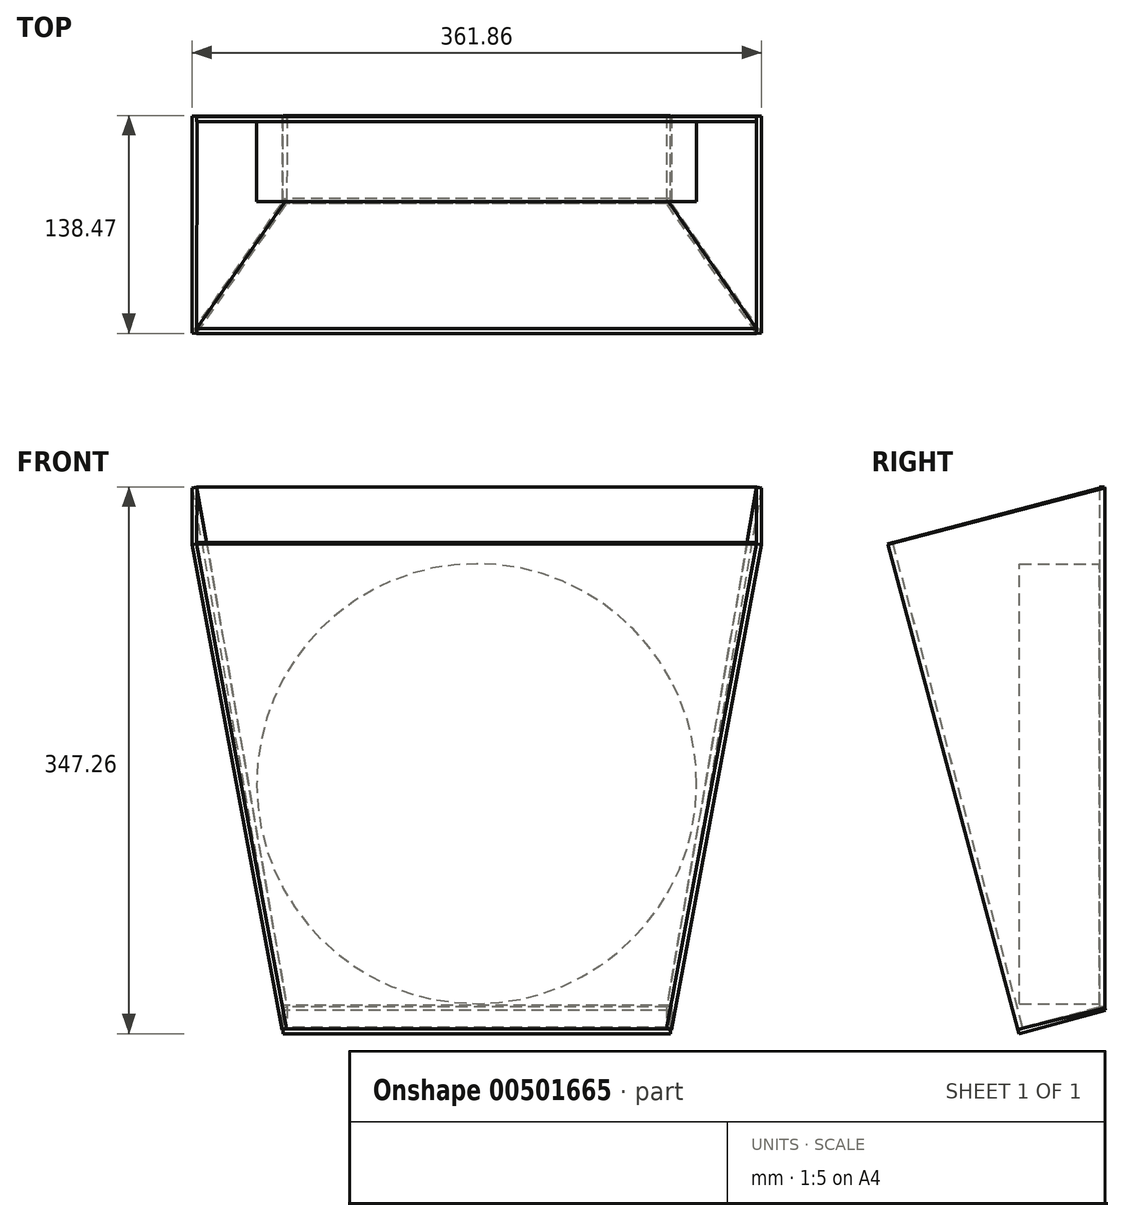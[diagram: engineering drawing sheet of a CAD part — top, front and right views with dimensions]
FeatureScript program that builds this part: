
annotation { "Feature Type Name" : "Feature", "Feature Type Description" : "" }
export const myFeature = defineFeature(function(context is Context, id is Id, definition is map)
    precondition{}
    {
        {
            var Q0;
            Q0=qCreatedBy(makeId("Right.planeOp"),FACE);
            var sketch = newSketch(context, id + "F0", { "sketchPlane" : qUnion([Q0])});
            skLineSegment(sketch, "E0.bottom", {"start": v(-164.52, 79.35) * mm, "end": v(-89.48, 66.12) * mm});
            skLineSegment(sketch, "E0.top", {"start": v(-67.49, 629.66) * mm, "end": v(7.56, 616.43) * mm});
            skLineSegment(sketch, "E0.left", {"start": v(-164.52, 79.35) * mm, "end": v(-67.49, 629.66) * mm});
            skLineSegment(sketch, "E0.right", {"start": v(-89.48, 66.12) * mm, "end": v(7.56, 616.43) * mm});
            skLineSegment(sketch, "E1.bottom", {"start": v(0, 38.1) * mm, "end": v(406.4, 38.1) * mm});
            skLineSegment(sketch, "E1.top", {"start": v(0, 546.1) * mm, "end": v(406.4, 546.1) * mm});
            skLineSegment(sketch, "E1.left", {"start": v(0, 38.1) * mm, "end": v(0, 546.1) * mm});
            skLineSegment(sketch, "E1.right", {"start": v(406.4, 38.1) * mm, "end": v(406.4, 546.1) * mm});
            skLineSegment(sketch, "E2.bottom", {"start": v(42.48, 128.48) * mm, "end": v(86.93, 128.48) * mm});
            skLineSegment(sketch, "E2.top", {"start": v(42.48, 84.03) * mm, "end": v(86.93, 84.03) * mm});
            skLineSegment(sketch, "E2.left", {"start": v(42.48, 128.48) * mm, "end": v(42.48, 84.03) * mm});
            skLineSegment(sketch, "E2.right", {"start": v(86.93, 128.48) * mm, "end": v(86.93, 84.03) * mm});
            skPoint(sketch, "E2.middle", {"position": v(64.7, 106.26) * mm});
            skSolve(sketch);
        }
        {
            var Q0;
            Q0=qCreatedBy(makeId("Front.planeOp"),FACE);
            var sketch = newSketch(context, id + "F1", { "sketchPlane" : qUnion([Q0])});
            skLineSegment(sketch, "E3.bottom", {"start": v(177.8, 596.9) * mm, "end": v(-177.8, 596.9) * mm});
            skLineSegment(sketch, "E3.top", {"start": v(120.65, 266.7) * mm, "end": v(-120.65, 266.7) * mm});
            skPoint(sketch, "E3.middle", {"position": v(0, 431.8) * mm});
            skLineSegment(sketch, "E4", {"start": v(-177.8, 596.9) * mm, "end": v(-120.65, 266.7) * mm});
            skLineSegment(sketch, "E5", {"start": v(0, 596.9) * mm, "end": v(0, 604.14) * mm, "construction": true});
            skPoint(sketch, "E5.endSnap0", {"position": v(0, 596.9) * mm});
            skLineSegment(sketch, "E6.MirrorCS", {"start": v(177.8, 596.9) * mm, "end": v(120.65, 266.7) * mm});
            skCircle(sketch, "E7", {"center": v(0, 408.44) * mm, "radius": 139.7 * mm, "construction": true});
            skCircle(sketch, "E8", {"center": v(0, 330.2) * mm, "radius": 17.46 * mm, "construction": true});
            skPoint(sketch, "E3.left.end.orphan", {"position": v(177.8, 266.7) * mm});
            skPoint(sketch, "E9.orphan", {"position": v(-177.8, 266.7) * mm});
            skSolve(sketch);
        }
        {
            var Q0;
            Q0=qSketchRegion(id+"F1",true);
            extrude(context, id + "F2", {"entities" : qUnion([Q0]), "oppositeDirection" : true, "depth" : 3.17 * mm});
        }
        {
            var Q0;
            Q0=makeQuery(id+"F1.imprint","IMPRINT",FACE,{"disambiguationData":[TD([[makeQuery(id+"F1.imprint","IMPRINT",EDGE,{"derivedFrom":sQuery(id+"F1.wireOp",EDGE,"E3.bottom")}),1.0]])]});
            var sketch = newSketch(context, id + "F3", { "sketchPlane" : qUnion([Q0])});
            skCircle(sketch, "E10.0", {"center": v(0, 408.44) * mm, "radius": 139.7 * mm});
            skSolve(sketch);
        }
        {
            var Q0;
            Q0=qSketchRegion(id+"F3",true);
            extrude(context, id + "F4", {"entities" : qUnion([Q0]), "depth" : 50.8 * mm});
        }
        {
            var Q0;
            Q0=makeQuery(id+"F4.opExtrude","CAP_FACE",FACE,{"disambiguationData":[OSD([sQuery(id+"F3.wireOp",EDGE,"E10.0")])],"isStart":false});
            var Q1;
            Q1=sQuery(id+"F1.wireOp",EDGE,"E3.top");
            cPlane(context, id + "F5", {"entities" : qUnion([Q0, Q1]), "cplaneType" : CPlaneType.LINE_ANGLE, "offset" : 25.4 * mm, "angle" : 345 * degree, "width" : 152.4 * mm, "height" : 152.4 * mm});
        }
        {
            var Q0;
            Q0=qCreatedBy(id+"F5.planeOp",FACE);
            cPlane(context, id + "F6", {"entities" : qUnion([Q0]), "cplaneType" : CPlaneType.OFFSET, "offset" : 53.97 * mm, "oppositeDirection" : true, "width" : 152.4 * mm, "height" : 152.4 * mm});
        }
        {
            var Q0;
            Q0=qCreatedBy(id+"F6.planeOp",FACE);
            var sketch = newSketch(context, id + "F7", { "sketchPlane" : qUnion([Q0])});
            skLineSegment(sketch, "E11.0", {"start": v(177.8, 576.56) * mm, "end": v(120.65, 257.61) * mm});
            skLineSegment(sketch, "E11.1", {"start": v(-177.8, 576.56) * mm, "end": v(177.8, 576.56) * mm});
            skLineSegment(sketch, "E11.2", {"start": v(-177.8, 576.56) * mm, "end": v(-120.65, 257.61) * mm});
            skLineSegment(sketch, "E11.3", {"start": v(-120.65, 257.61) * mm, "end": v(120.65, 257.61) * mm});
            skSolve(sketch);
        }
        {
            var Q0;
            Q0=makeQuery(id+"F7.imprint","IMPRINT",FACE,{"disambiguationData":[TD([[makeQuery(id+"F7.imprint","IMPRINT",EDGE,{"derivedFrom":sQuery(id+"F7.wireOp",EDGE,"E11.0")}),-1.0]])]});
            extrude(context, id + "F8", {"entities" : qUnion([Q0]), "depth" : 3.17 * mm});
        }
        {
            var Q0;
            Q0=makeQuery(id+"F8.opExtrude","SWEPT_FACE",FACE,{"disambiguationData":[OSD([sQuery(id+"F7.wireOp",EDGE,"E11.0")])]});
            var sketch = newSketch(context, id + "F9", { "sketchPlane" : qUnion([Q0])});
            skLineSegment(sketch, "E12.0", {"start": v(0.18, 618.48) * mm, "end": v(0.18, 283.37) * mm});
            skLineSegment(sketch, "E13.0", {"start": v(138.18, 582.92) * mm, "end": v(55.54, 269.6) * mm});
            skLineSegment(sketch, "E14", {"start": v(0.18, 283.37) * mm, "end": v(52.47, 270.41) * mm});
            skLineSegment(sketch, "E15", {"start": v(0.18, 618.48) * mm, "end": v(138.18, 582.92) * mm});
            skSolve(sketch);
        }
        {
            var Q0;
            {var subQ0=sQuery(id+"F9.wireOp",EDGE,"E12.0");Q0=makeQuery(id+"F9.imprint","IMPRINT",FACE,{"disambiguationData":[TD([[makeQuery(id+"F9.imprint","IMPRINT",EDGE,{"derivedFrom":subQ0}),1.0]])]});}
            var Q1;
            {var subQ0=sQuery(id+"F9.wireOp",EDGE,"E13.0");Q1=makeQuery(id+"F9.imprint","IMPRINT",FACE,{"disambiguationData":[TD([[makeQuery(id+"F9.imprint","IMPRINT",EDGE,{"derivedFrom":subQ0}),-1.0]])]});}
            extrude(context, id + "F10", {"entities" : qUnion([Q0, Q1]), "depth" : 3.17 * mm});
        }
        {
            var Q0;
            Q0=makeQuery(id+"F10.opExtrude","SWEPT_BODY",BODY,{"disambiguationData":[OSD([sQuery(id+"F7.wireOp",EDGE,"E11.0"),sQuery(id+"F9.wireOp",EDGE,"E12.0"),sQuery(id+"F9.wireOp",EDGE,"E14"),sQuery(id+"F9.wireOp",EDGE,"E15")])]});
            var Q1;
            Q1=qCreatedBy(makeId("Right.planeOp"),FACE);
            mirror(context, id + "F11", {"entities" : qUnion([Q0]), "mirrorPlane" : qUnion([Q1])});
        }
        {
            var Q0;
            Q0=makeQuery(id+"F8.opExtrude","SWEPT_FACE",FACE,{"disambiguationData":[OSD([sQuery(id+"F7.wireOp",EDGE,"E11.3")])]});
            var sketch = newSketch(context, id + "F12", { "sketchPlane" : qUnion([Q0])});
            skLineSegment(sketch, "E16.bottom", {"start": v(122.9, -15.05) * mm, "end": v(-122.9, -15.05) * mm});
            skLineSegment(sketch, "E16.top", {"start": v(122.9, -72.1) * mm, "end": v(-122.9, -72.1) * mm});
            skLineSegment(sketch, "E16.left", {"start": v(122.9, -15.05) * mm, "end": v(122.9, -72.1) * mm});
            skLineSegment(sketch, "E16.right", {"start": v(-122.9, -15.05) * mm, "end": v(-122.9, -72.1) * mm});
            skPoint(sketch, "E16.middle", {"position": v(0, -43.57) * mm});
            skSolve(sketch);
        }
        {
            var Q0;
            Q0=qSketchRegion(id+"F12",true);
            extrude(context, id + "F13", {"entities" : qUnion([Q0]), "depth" : 3.17 * mm});
        }
    });
